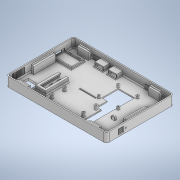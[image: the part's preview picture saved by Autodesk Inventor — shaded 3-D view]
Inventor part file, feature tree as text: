
AUTODESK INVENTOR PART (.ipt)
format: ipt  version: 2021 (Build 250183000, 183)  size: 1,250,304 bytes
history: native  units: mm
features: extrude x39, sketch x33, projected_geometry x29, chamfer x12, mirror x9, plane x5, fillet x2, hole x2, shell x1, pattern_linear x1
ambient origin geometry x8: Origin, YZ Plane, XZ Plane, XY Plane, X Axis, Y Axis, Z Axis, Center Point
bodies: Solid1 (feature_tree)
feature tree (133):
  extrude  "Extrusion1"  Depth=124.0mm
  fillet  "Fillet1"  Radius=17.0mm
  shell  "Shell1"  Thickness=5.0mm
  plane  "Work Plane4"
  extrude  "Extrusion21"  Depth=20.0mm
  fillet  "Fillet3"  Radius=8.0mm
  plane  "Work Plane5"
  sketch  "Sketch31"  dims[d5=2.0mm d151=20.0mm d152=8.0mm]
  extrude  "Extrusion22"  Depth=5.0mm
  extrude  "Extrusion23"  Depth=1.972163mm
  extrude  "Extrusion24"  Depth=10.5mm
  extrude  "Extrusion25"  Depth=111.9mm
  mirror  "Mirror13"
  extrude  "Extrusion27"  Depth=5.0mm
  extrude  "Extrusion28"  [1 undecoded]
  extrude  "Extrusion29"  Depth=1.2mm TaperAngle=0.0deg
  sketch  "Sketch36"  dims[d185=3.0mm d186=0.0mm d187=10.5mm]
  extrude  "Extrusion30"  Depth=5.0mm
  extrude  "Extrusion31"  Depth=1.2mm TaperAngle=0.0deg
  extrude  "Extrusion26"  Depth=30.404mm
  hole  "Hole10"  [1 undecoded]
  hole  "Hole11"  [1 undecoded]
  plane  "Work Plane8"
  plane  "Work Plane9"
  mirror  "Mirror14"
  mirror  "Mirror15"
  extrude  "Extrusion32"  Depth=65.0mm
  mirror  "Mirror16"
  mirror  "Mirror17"
  extrude  "Extrusion33"  Depth=6.0mm
  chamfer  "Chamfer6"  Distance=6.0mm
  plane  "Work Plane10"
  extrude  "Extrusion40"  TaperAngle=0.0deg  [1 undecoded]
  extrude  "Extrusion45"  Depth=60.0mm
  extrude  "Extrusion46"  Depth=15.24mm
  extrude  "Extrusion47"  Depth=13.5mm
  chamfer  "Chamfer7"  Distance=4.0mm
  extrude  "Extrusion48"  Depth=3.0mm
  mirror  "Mirror22"
  mirror  "Mirror23"
  sketch  "Sketch61"  dims[d210=43.0mm d211=65.0mm]
  extrude  "Extrusion49"  TaperAngle=90.0deg  [1 undecoded]
  sketch  "Sketch63"  dims[d214=3.5mm]
  extrude  "Extrusion51"  Depth=12.0mm
  extrude  "Extrusion52"  Depth=1.2mm TaperAngle=0.0deg
  sketch  "Sketch65"  dims[d216=6.0mm]
  extrude  "Extrusion53"  Depth=12.0mm
  extrude  "Extrusion54"  Depth=2.0mm
  extrude  "Extrusion55"  Depth=1.2mm TaperAngle=0.0deg
  extrude  "Extrusion56"  Depth=2.0mm TaperAngle=45.0deg
  chamfer  "Chamfer8"  [1 undecoded]
  chamfer  "Chamfer9"  Distance=13.2mm
  extrude  "Extrusion57"  Depth=5.7mm
  chamfer  "Chamfer10"  Distance=52.0mm
  chamfer  "Chamfer11"  Distance=20.0mm
  extrude  "Extrusion58"  Depth=4.0mm TaperAngle=0.0deg
  extrude  "Extrusion60"  Depth=1.5mm
  mirror  "Mirror24"
  chamfer  "Chamfer12"  Distance=1.5mm
  chamfer  "Chamfer13"  Distance=13.2mm
  chamfer  "Chamfer14"  Distance=0.6mm
  mirror  "Mirror25"
  extrude  "Extrusion62"  Depth=0.6mm
  extrude  "Extrusion63"  Depth=0.5mm TaperAngle=0.0deg
  extrude  "Extrusion64"  Depth=20.4mm
  chamfer  "Chamfer15"  Distance=41.0mm
  chamfer  "Chamfer16"  Distance=3.0mm
  extrude  "Extrusion65"  Depth=3.0mm
  extrude  "Extrusion66"  Depth=2.0mm TaperAngle=45.0deg
  extrude  "Extrusion67"  Depth=2.0mm
  pattern_linear  "Rectangular Pattern1"  Spacing1=0.0mm  [1 undecoded]
  extrude  "Extrusion68"  Depth=33.3mm
  chamfer  "Chamfer18"  Distance=1.0mm
  extrude  "Extrusion72"  Depth=18.0mm
  extrude  "Extrusion73"  Depth=20.7mm
  extrude  "Extrusion74"  Depth=5.0mm
  sketch  "Sketch1"  dims[d0=184.4mm d1=124.0mm d2=17.0mm d3=0.0mm d4=5.0mm]
  sketch  "Sketch33"  dims[d153=30.0mm d156=5.0mm]
  sketch  "Sketch35"  dims[d157=4.021107mm d158=1.972163mm]
  sketch  "Sketch37"  dims[d188=170.4mm d189=111.9mm]
  sketch  "Sketch38"  dims[d190=20.0mm d191=5.0mm]
  sketch  "Sketch40"  dims[d192=10.0mm d193=-1.0mm]
  projected_geometry  "Projected Loop1"
  sketch  "Sketch44"  dims[d194=1.2mm d195=0.0mm d196=1.2mm d197=0.0mm]
  projected_geometry  "Projected Loop2"
  sketch  "Sketch50"  dims[d198=40.0mm d199=5.0mm]
  sketch  "Sketch53"  dims[d200=1.2mm d201=0.0mm d202=1.2mm d203=0.0mm]
  sketch  "Sketch57"  dims[d204=30.429mm d205=30.404mm]
  sketch  "Sketch58"  dims[d206=5.004mm d207=2.502mm]
  sketch  "Sketch60"  dims[d208=2.502mm d209=25.0mm]
  sketch  "Sketch62"  dims[d212=30.2mm d213=6.0mm]
  sketch  "Sketch64"  dims[d215=3.5mm]
  projected_geometry  "Projected Loop3"
  sketch  "Sketch66"  dims[d217=3.5mm]
  projected_geometry  "Projected Loop4"
  projected_geometry  "Projected Loop5"
  projected_geometry  "Projected Loop6"
  sketch  "Sketch68"  dims[d218=3.7mm d221=6.0mm d222=0.0mm]
  sketch  "Sketch69"  dims[d223=4.0mm d224=0.0mm d225=0.0mm d226=0.0mm]
  projected_geometry  "Projected Loop7"
  projected_geometry  "Projected Loop8"
  sketch  "Sketch71"  dims[d227=12.0mm d228=60.0mm]
  sketch  "Sketch72"  dims[d229=0.0mm d230=0.0mm d231=15.24mm]
  sketch  "Sketch75"  dims[d232=13.5mm d233=2.55mm]
  projected_geometry  "Projected Loop9"
  sketch  "Sketch76"  dims[d234=15.24mm]
  sketch  "Sketch77"  dims[d235=2.54mm d238=4.0mm d239=0.0mm]
  projected_geometry  "Projected Loop10"
  sketch  "Sketch79"  dims[d240=0.0mm d241=0.0mm]
  sketch  "Sketch80"  dims[d242=3.0mm d243=6.0mm d244=4.0mm d245=2.0mm d246=90.0deg d247=8.0mm d248=20.594885mm]
  sketch  "Sketch81"  dims[d249=2.0mm d250=6.0mm d251=4.0mm d252=2.0mm d253=90.0deg d254=8.0mm d255=20.594885mm d256=3.0mm]
  sketch  "Sketch85"  dims[d258=90.0deg d259=90.0deg]
  sketch  "Sketch86"  dims[d260=2.0mm d261=12.0mm]
  sketch  "Sketch87"  dims[d262=39.0mm d264=1.2mm d265=0.0mm d266=12.0mm d267=2.0mm d270=1.2mm d271=0.0mm d330=2.0mm d331=0.2mm d332=45.0deg d335=0.0mm d336=0.0mm d361=13.2mm d362=5.7mm d363=52.0mm d364=20.0mm d366=24.0mm d367=10.0mm d369=10.0mm d377=4.0mm d378=0.0mm d379=1.5mm d380=1.5mm d381=13.2mm d382=0.0mm d383=0.6mm d384=0.6mm d385=0.5mm d386=0.0mm d387=20.4mm d388=41.0mm d389=3.0mm d390=3.0mm d391=2.0mm d392=2.0mm d393=45.0deg d395=2.0mm d396=0.0mm d397=0.0mm d398=33.3mm d399=1.0mm d400=18.0mm d401=20.7mm d403=5.0mm d404=1.0mm d405=0.0mm d406=4.0mm d407=5.0mm d408=6.5mm d411=1.5mm d412=0.0mm d413=0.0mm d414=1.0mm d415=1.0mm d416=1.5mm d417=0.0mm d418=2.0mm d419=2.0mm d420=2.0mm d421=0.0mm d422=0.0mm d423=4.2mm d424=0.0mm d425=3.2mm d426=0.0mm d427=6.0mm d428=1.0mm d429=1.0mm d430=6.0mm d431=6.0mm d432=6.0mm d433=0.2mm d434=0.0mm d435=1.0mm d436=0.2mm d437=45.0deg d438=1.0mm d439=0.2mm d440=45.0deg d441=0.2mm d442=0.0mm d443=1.0mm d444=0.2mm d445=45.0deg d446=1.0mm d447=0.2mm d448=45.0deg d449=2.5mm d450=19.0mm d451=11.5mm d452=2.5mm d453=9.5mm d454=10.0mm d455=1.9mm d456=16.0mm d457=0.2mm d458=0.0mm d461=2.0mm d462=35.17484mm d463=2.0mm d464=0.0mm d465=2.0mm d466=1.0mm d467=0.2mm d468=45.0deg d469=1.0mm d470=0.2mm d471=45.0deg d472=1.0mm d473=0.2mm d474=45.0deg d502=2.0mm d503=1.8mm d504=2.0mm d505=2.0mm d506=1.5mm d507=0.0mm d508=8.0mm d510=8.0mm d511=12.0mm d512=15.0mm d513=0.5mm d514=0.0mm d515=1.5mm d516=11.0mm d517=1.0mm d518=120.0mm d520=2.0mm d521=10.0mm d523=10.0mm d525=0.0mm d526=0.0mm d527=0.4mm d528=2.0mm d529=45.0deg d530=1.0mm d531=2.0mm d532=45.0deg d533=2.0mm d534=30.0mm d535=60.03mm d536=0.0mm d537=0.0mm d538=6.2mm d539=6.2mm d540=1.0mm d541=0.0mm d542=3.6mm d543=0.0mm d544=0.0mm d545=30.0mm d547=14.2mm d556=40.0mm d557=16.9mm d558=16.9mm d560=7.0mm d561=0.0mm d562=40.0mm d563=16.9mm d564=2.0mm d565=4.0mm d566=4.0mm d580=2.0mm d581=2.0mm d582=2.0mm d583=2.0mm d584=45.0deg d585=2.0mm d586=2.0mm d587=0.0mm d588=2.0mm d589=2.0mm d590=0.0mm d591=2.0mm d592=2.0mm d593=0.0mm d14=0.5mm d15=0.872665mm d16=0.5mm d17=0.872665mm d127=0.5mm d128=0.872665mm d129=0.5mm d130=0.872665mm d135=1.0mm d136=1.0mm d137=1.0mm d138=0.15mm d139=0.25mm d140=0.375mm d141=14.3117mm d142=0.75mm d143=20.594885mm d144=0.0625mm d145=0.75mm d146=0.375mm d159=0.5mm d160=0.872665mm d257=20.594885mm]
  projected_geometry  "Project Cut Edges2"
  projected_geometry  "Project Cut Edges3"
  projected_geometry  "Project Cut Edges5"
  projected_geometry  "Project Cut Edges6"
  projected_geometry  "Project Cut Edges7"
  projected_geometry  "Project Cut Edges8"
  projected_geometry  "Project Cut Edges9"
  projected_geometry  "Project Cut Edges10"
  projected_geometry  "Project Cut Edges11"
  projected_geometry  "Project Cut Edges12"
  projected_geometry  "Project Cut Edges13"
  projected_geometry  "Project Cut Edges14"
  projected_geometry  "Project Cut Edges15"
  projected_geometry  "Project Cut Edges16"
  projected_geometry  "Project Cut Edges17"
  projected_geometry  "Project Cut Edges18"
  projected_geometry  "Project Cut Edges19"
  projected_geometry  "Project Cut Edges20"
  projected_geometry  "Project Cut Edges21"
note: 7 required parameter values undecoded (feature->parameter linkage not recoverable at this tier; creation-order binding heuristic only, values carry confidence <= 0.55)
